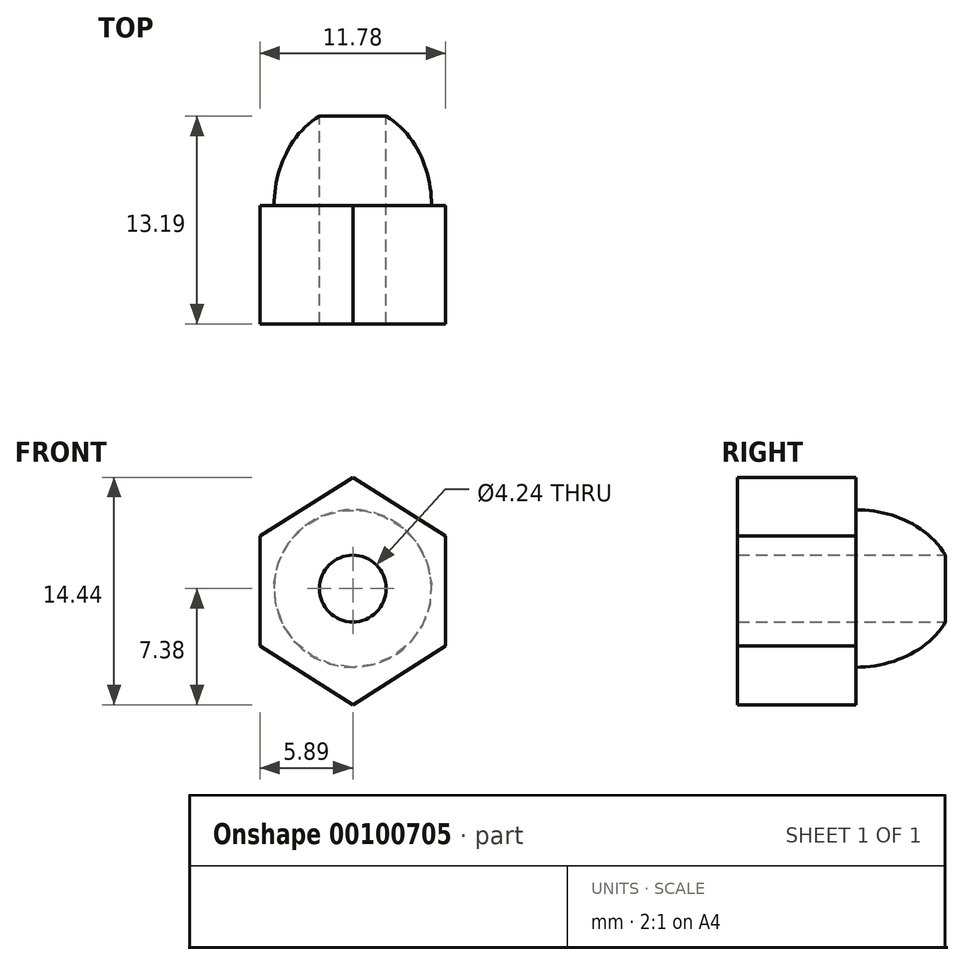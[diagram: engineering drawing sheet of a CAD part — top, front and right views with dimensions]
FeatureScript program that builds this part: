
annotation { "Feature Type Name" : "Feature", "Feature Type Description" : "" }
export const myFeature = defineFeature(function(context is Context, id is Id, definition is map)
    precondition{}
    {
        {
            var Q0;
            Q0=qCreatedBy(makeId("Right.planeOp"),FACE);
            var sketch = newSketch(context, id + "F0", { "sketchPlane" : qUnion([Q0])});
            skLineSegment(sketch, "E0", {"start": v(0, 0) * mm, "end": v(-7.5, 0) * mm});
            skLineSegment(sketch, "E1", {"start": v(-7.5, 0) * mm, "end": v(-7.5, 5) * mm});
            skLineSegment(sketch, "E2", {"start": v(-7.5, 5) * mm, "end": v(0, 5) * mm});
            skEllipticalArc(sketch, "E3", {});
            skLineSegment(sketch, "E4", {"start": v(0, 0) * mm, "end": v(6.29, 0) * mm});
            const initialGuessF0  = {"E3": [0, 0, 0.9999999284102867, -0.000378390567379781, 0.0062885531069654665, 0.004999999868338198, 0.0004759058463017495, 1.5712722326411983]};
            skSetInitialGuess(sketch, initialGuessF0);
            skSolve(sketch);
        }
        {
            var Q0;
            Q0=qCreatedBy(makeId("Right.planeOp"),FACE);
            var sketch = newSketch(context, id + "F3", { "sketchPlane" : qUnion([Q0])});
            skLineSegment(sketch, "E5", {"start": v(-45.69, 0) * mm, "end": v(38.02, 0) * mm});
            skSolve(sketch);
        }
        {
            var Q0;
            Q0 = qSketchRegion(id + "F0", true);
            var Q1;
            Q1 = qBodyType(qCreatedBy(id + "F3" ,EDGE), BodyType.WIRE);
            revolve(context, id + "F4", {"entities" : qUnion([Q0]), "axis" : qUnion([Q1]), "revolveType" : RevolveType.FULL});
        }
        {
            var Q0;
            Q0=makeQuery(id+"F4.opRevolve","SWEPT_FACE",FACE,{"disambiguationData":[OSD([sQuery(id+"F0.wireOp",EDGE,"E1")])]});
            var sketch = newSketch(context, id + "F5", { "sketchPlane" : qUnion([Q0])});
            skLineSegment(sketch, "E6", {"start": v(0, 0) * mm, "end": v(0, 7.06) * mm, "construction": true});
            skLineSegment(sketch, "E7", {"start": v(0, 7.06) * mm, "end": v(-5.89, 3.33) * mm});
            skLineSegment(sketch, "E8", {"start": v(-5.89, 3.33) * mm, "end": v(-5.89, -3.65) * mm});
            skLineSegment(sketch, "E9", {"start": v(-5.89, -3.65) * mm, "end": v(0, -7.38) * mm});
            skLineSegment(sketch, "E10", {"start": v(0, -7.38) * mm, "end": v(5.89, -3.65) * mm});
            skLineSegment(sketch, "E11", {"start": v(5.89, -3.65) * mm, "end": v(5.89, 3.33) * mm});
            skLineSegment(sketch, "E12", {"start": v(5.89, 3.33) * mm, "end": v(0, 7.06) * mm});
            skLineSegment(sketch, "E13", {"start": v(-5.89, -3.65) * mm, "end": v(5.89, -3.65) * mm, "construction": true});
            skLineSegment(sketch, "E14", {"start": v(-5.89, 3.33) * mm, "end": v(5.89, 3.33) * mm, "construction": true});
            skSolve(sketch);
        }
        {
            var Q0;
            Q0 = qSketchRegion(id + "F5", true);
            extrude(context, id + "F1", {"entities" : qUnion([Q0]), "operationType" : NewBodyOperationType.ADD, "oppositeDirection" : true, "depth" : 7.5 * mm});
        }
        {
            var Q0;
            Q0=makeQuery(id+"F1.boolean.opBoolean","MERGE",FACE,{"derivedFrom":[makeQuery(id+"F4.opRevolve","SWEPT_FACE",FACE,{"disambiguationData":[OSD([sQuery(id+"F0.wireOp",EDGE,"E1")])]}),makeQuery(id+"F1.opExtrude","CAP_FACE",FACE,{"disambiguationData":[OSD([sQuery(id+"F5.wireOp",EDGE,"E7"),sQuery(id+"F5.wireOp",EDGE,"E8"),sQuery(id+"F5.wireOp",EDGE,"E9"),sQuery(id+"F5.wireOp",EDGE,"E10"),sQuery(id+"F5.wireOp",EDGE,"E11"),sQuery(id+"F5.wireOp",EDGE,"E12")])],"isStart":true})]});
            var sketch = newSketch(context, id + "F2", { "sketchPlane" : qUnion([Q0])});
            skPoint(sketch, "E15", {"position": v(0, 0) * mm});
            skSolve(sketch);
        }
        {
            var Q0;
            Q0=sQuery(id+"F2.wireOp",VERTEX,"E15");
            var Q1;
            Q1=makeQuery(id+"F4.opRevolve","SWEPT_BODY",BODY,{"disambiguationData":[OSD([sQuery(id+"F0.wireOp",EDGE,"E0"),sQuery(id+"F0.wireOp",EDGE,"E1"),sQuery(id+"F0.wireOp",EDGE,"E2"),sQuery(id+"F0.wireOp",EDGE,"E3"),sQuery(id+"F0.wireOp",EDGE,"E4")])]});
            hole(context, id + "F6", {"style" : HoleStyle.SIMPLE, "endStyle" : HoleEndStyle.THROUGH, "holeDiameter" : 4.24 * mm, "locations" : qUnion([Q0]), "scope" : qUnion([Q1]), "isTappedThrough" : true, "startStyle" : HoleStartStyle.PART});
        }
    });
